# Revit family: Haworth_Massimosistema_SofaBench_OneArm
name_source: partatom
category: Furniture
revit_build: Autodesk Revit 2018 (Build: 20170223_1515(x64)
units: mm (PartAtom-declared; Revit-internal decimal feet)

## family parameters
Always vertical = Yes
Cut with Voids When Loaded = No
OmniClass Number = 23.40.20.00
OmniClass Title = General Furniture and Specialties
Room Calculation Point = No
Shared = No
Work Plane-Based = No

## types (2) — shared parameters
Actual Depth = 39 1/4"
Actual Height = 33 3/4"
Assembly Code = E2020200
Bench = Yes
Frame Finish = Haworth _ Paint _ Metallic Gunmetal
Manufacturer = Haworth
Seat Height = 16 1/2"
Size = Verify Final Dim. w/ Haworth
URL = http://www.haworth.com
URL - Product = http://www.haworth.com
Version = 1
Warranty = https://www.haworth.com

## per-type parameters (varying)
| type | Actual Width | Arm Height | Arm Width | Back End w Arm | Cushion Width | Description | High | Low | One Seat | Seat Width | Total Seat Width | Two Seat Control | Two Seats |
| HCPF-MSSN | 103 1/2" | 28" | 6 3/4" | 39" | 32 1/4" | Haworth Massimosistema Sofa - High One Arm with Bench - Two Seats | Yes | No | No | 96 3/4" | 96 3/4" | No | Yes |
| HCPF-MSSB | 73 1/4" | 22 3/4" | 9 1/2" | 39 1/2" | 31 7/8" | Haworth Massimosistema Sofa - High One Arm with Bench - One Seat | No | Yes | Yes | 63 3/4" | 63 3/4" | Yes | No |

note: column(s) folded — value = type name in every type: Model

## geometry (parser evidence)
native form markers: Sweep x10
no freeform markers — native parametric forms only
